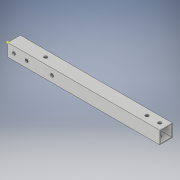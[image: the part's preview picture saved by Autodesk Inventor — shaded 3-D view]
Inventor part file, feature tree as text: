
AUTODESK INVENTOR PART (.ipt)
format: ipt  version: 2017 (Build 210142000, 142)  size: 130,048 bytes
history: native  units: in
note: dims shown in document units (in); Inventor stores cm internally (conversion verified against a paired STEP export)
features: sketch x4, extrude x3
ambient origin geometry x8: Origin, YZ Plane, XZ Plane, XY Plane, X Axis, Y Axis, Z Axis, Center Point
bodies: Solid1 (feature_tree)
feature tree (7):
  extrude  "Extrusion1"  Depth=1.0in
  extrude  "Extrusion2"  Depth=12.0in TaperAngle=0.0deg
  extrude  "Extrusion3"  Depth=0.5in
  sketch  "Sketch4"  dims[d7=1.0in d8=0.0in d9=1.5in d10=0.25in d11=0.5in d12=1.5in d13=3.5in d14=0.0in d15=2.5in d16=3.5in]
  sketch  "Sketch1"  dims[d0=1.0in d1=1.0in]
  sketch  "Sketch2"  dims[d2=0.0625in d3=12.0in d4=0.0in]
  sketch  "Sketch3"  dims[d5=0.25in d6=0.5in]
